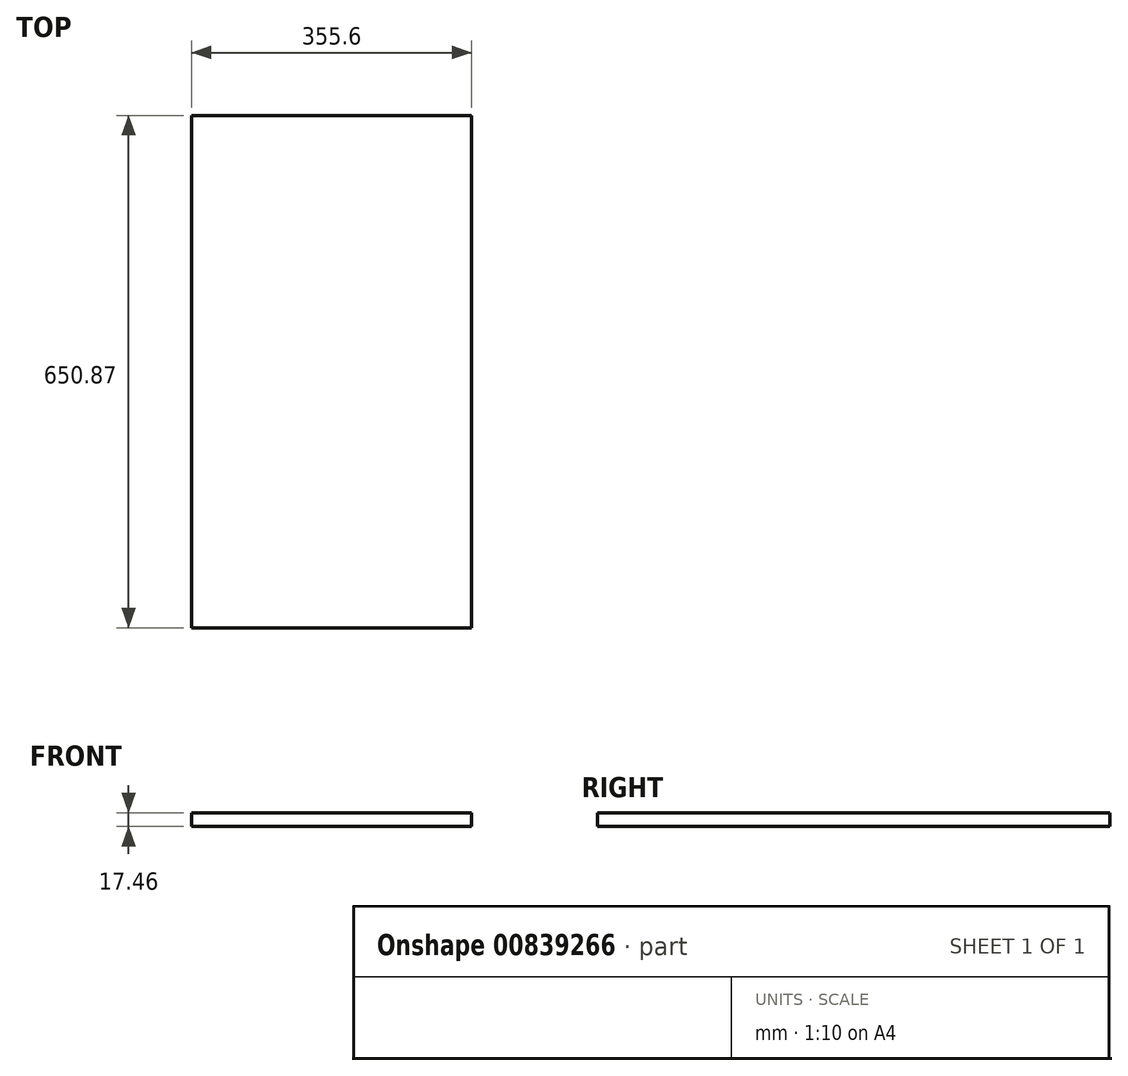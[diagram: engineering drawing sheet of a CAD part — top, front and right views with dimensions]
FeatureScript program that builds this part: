
annotation { "Feature Type Name" : "Feature", "Feature Type Description" : "" }
export const myFeature = defineFeature(function(context is Context, id is Id, definition is map)
    precondition{}
    {
        {
            var Q0;
            Q0=qCreatedBy(makeId("Top.planeOp"),FACE);
            var sketch = newSketch(context, id + "F0", { "sketchPlane" : qUnion([Q0])});
            skLineSegment(sketch, "E0.bottom", {"start": v(-207.76, 436.97) * mm, "end": v(147.84, 436.97) * mm});
            skLineSegment(sketch, "E0.top", {"start": v(-207.76, -213.9) * mm, "end": v(147.84, -213.9) * mm});
            skLineSegment(sketch, "E0.left", {"start": v(-207.76, 436.97) * mm, "end": v(-207.76, -213.9) * mm});
            skLineSegment(sketch, "E0.right", {"start": v(147.84, 436.97) * mm, "end": v(147.84, -213.9) * mm});
            skSolve(sketch);
        }
        {
            var Q0;
            Q0 = qSketchRegion(id + "F0", true);
            extrude(context, id + "F1", {"entities" : qUnion([Q0]), "depth" : 17.46 * mm, "offsetDistance" : 25.4 * mm});
        }
    });
